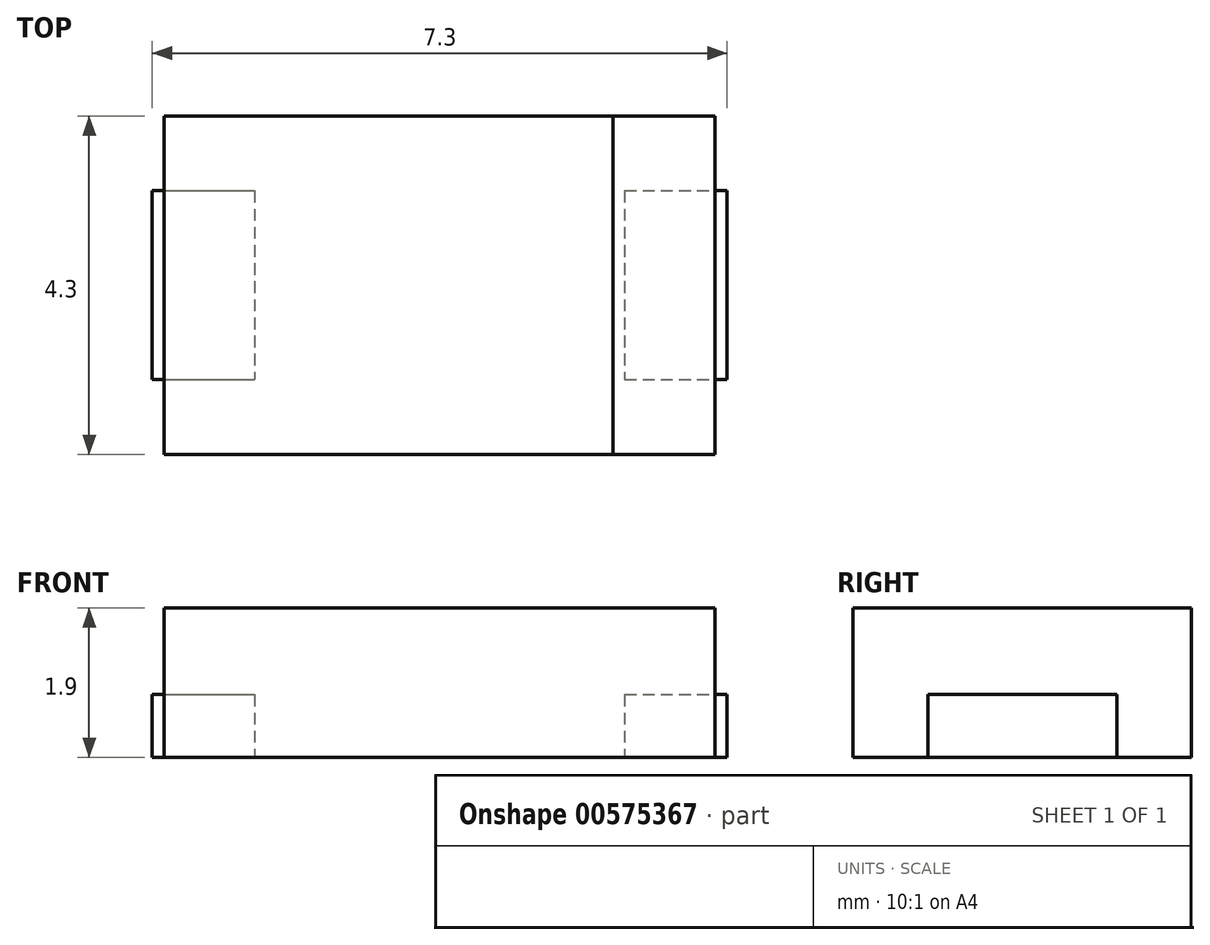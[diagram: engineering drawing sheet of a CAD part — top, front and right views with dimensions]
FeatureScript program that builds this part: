
annotation { "Feature Type Name" : "Feature", "Feature Type Description" : "" }
export const myFeature = defineFeature(function(context is Context, id is Id, definition is map)
    precondition{}
    {
        {
            var Q0;
            Q0=qCreatedBy(makeId("Top.planeOp"),FACE);
            var sketch = newSketch(context, id + "F0", { "sketchPlane" : qUnion([Q0])});
            skLineSegment(sketch, "E0.bottom", {"start": v(-3.65, 1.2) * mm, "end": v(-2.35, 1.2) * mm});
            skLineSegment(sketch, "E0.top", {"start": v(-3.65, -1.2) * mm, "end": v(-2.35, -1.2) * mm});
            skLineSegment(sketch, "E0.left", {"start": v(-3.65, 1.2) * mm, "end": v(-3.65, -1.2) * mm});
            skLineSegment(sketch, "E0.right", {"start": v(-2.35, 1.2) * mm, "end": v(-2.35, -1.2) * mm});
            skLineSegment(sketch, "E1.bottom", {"start": v(2.35, 1.2) * mm, "end": v(3.65, 1.2) * mm});
            skLineSegment(sketch, "E1.top", {"start": v(2.35, -1.2) * mm, "end": v(3.65, -1.2) * mm});
            skLineSegment(sketch, "E1.left", {"start": v(2.35, 1.2) * mm, "end": v(2.35, -1.2) * mm});
            skLineSegment(sketch, "E1.right", {"start": v(3.65, 1.2) * mm, "end": v(3.65, -1.2) * mm});
            skSolve(sketch);
        }
        {
            var Q0;
            Q0 = qSketchRegion(id + "F0", true);
            extrude(context, id + "F1", {"entities" : qUnion([Q0]), "depth" : 0.8 * mm, "offsetDistance" : 25 * mm});
        }
        {
            var Q0;
            Q0=qCreatedBy(makeId("Top.planeOp"),FACE);
            var sketch = newSketch(context, id + "F2", { "sketchPlane" : qUnion([Q0])});
            skLineSegment(sketch, "E2.bottom", {"start": v(-3.5, 2.15) * mm, "end": v(3.5, 2.15) * mm});
            skLineSegment(sketch, "E2.top", {"start": v(-3.5, -2.15) * mm, "end": v(3.5, -2.15) * mm});
            skLineSegment(sketch, "E2.left", {"start": v(-3.5, 2.15) * mm, "end": v(-3.5, -2.15) * mm});
            skLineSegment(sketch, "E2.right", {"start": v(3.5, 2.15) * mm, "end": v(3.5, -2.15) * mm});
            skSolve(sketch);
        }
        {
            var Q0;
            Q0 = qSketchRegion(id + "F2", true);
            extrude(context, id + "F3", {"entities" : qUnion([Q0]), "depth" : 1.9 * mm, "offsetDistance" : 25 * mm});
        }
        {
            var Q0;
            Q0=makeQuery(id+"F3.opExtrude","CAP_FACE",FACE,{"disambiguationData":[OSD([sQuery(id+"F2.wireOp",EDGE,"E2.bottom"),sQuery(id+"F2.wireOp",EDGE,"E2.top"),sQuery(id+"F2.wireOp",EDGE,"E2.left"),sQuery(id+"F2.wireOp",EDGE,"E2.right")])],"isStart":false});
            var sketch = newSketch(context, id + "F4", { "sketchPlane" : qUnion([Q0])});
            skLineSegment(sketch, "E3.bottom", {"start": v(3.5, 2.15) * mm, "end": v(2.2, 2.15) * mm});
            skLineSegment(sketch, "E3.top", {"start": v(3.5, -2.15) * mm, "end": v(2.2, -2.15) * mm});
            skLineSegment(sketch, "E3.left", {"start": v(3.5, 2.15) * mm, "end": v(3.5, -2.15) * mm});
            skLineSegment(sketch, "E3.right", {"start": v(2.2, 2.15) * mm, "end": v(2.2, -2.15) * mm});
            skSolve(sketch);
        }
        {
            var Q0;
            Q0 = qSketchRegion(id + "F4", true);
            extrude(context, id + "F5", {"entities" : qUnion([Q0]), "depth" : 0 * mm, "offsetDistance" : 25 * mm});
        }
    });
